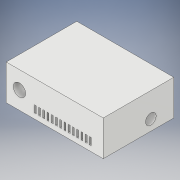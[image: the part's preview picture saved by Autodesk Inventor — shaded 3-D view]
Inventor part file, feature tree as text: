
AUTODESK INVENTOR PART (.ipt)
format: ipt  version: 2017 SP1 (Build 210196100, 196)  size: 176,640 bytes
history: native  units: in
note: dims shown in document units (in); Inventor stores cm internally (conversion verified against a paired STEP export)
features: extrude x3, sketch x3
ambient origin geometry x8: Origin, YZ Plane, XZ Plane, XY Plane, X Axis, Y Axis, Z Axis, Center Point
bodies: Solid1 (feature_tree)
feature tree (6):
  extrude  "Extrusion1"  Depth=0.3937in
  extrude  "Extrusion2"  Depth=0.7874in
  extrude  "Extrusion3"  Depth=0.1378in
  sketch  "Sketch1"  dims[d0=1.0827in d1=0.3937in]
  sketch  "Sketch2"  dims[d2=0.7874in d3=0.0in d4=0.1969in]
  sketch  "Sketch3"  dims[d5=0.1476in d6=0.1378in d7=0.0197in d8=0.0787in d9=0.1339in d10=0.0591in d11=5.5118in d13=0.0472in d14=0.3937in d16=0.3937in d18=0.1181in d19=0.0in d20=0.1181in d21=0.2559in d22=0.1181in d23=0.1969in d24=0.0in]
